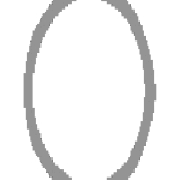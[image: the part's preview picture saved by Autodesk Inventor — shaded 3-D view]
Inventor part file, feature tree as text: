
AUTODESK INVENTOR PART (.ipt)
format: ipt  version: 2021 (Build 250183000, 183)  size: 110,592 bytes
history: native  units: in
note: dims shown in document units (in); Inventor stores cm internally (conversion verified against a paired STEP export)
features: other x4, sketch x3, plane x1
ambient origin geometry x8: Origin, YZ Plane, XZ Plane, XY Plane, X Axis, Y Axis, Z Axis, Center Point
bodies: Solid1 (feature_tree), Body (feature_tree)
feature tree (8):
  other  "Driven Length"
  other  "Frame Generator"
  other  "Start Plane"
  other  "End Plane"
  sketch  "Sketch"  dims[d2=8.3217in d4=-0.0in d5=8.3217in d6=0.12in d7=0.0in d8=90.0deg d9=8.3217in]
  sketch  "Sketch2"  dims[d0=1.0in]
  plane  "Work Plane3"
  sketch  "Sketch3"  dims[d1=0.065in]
